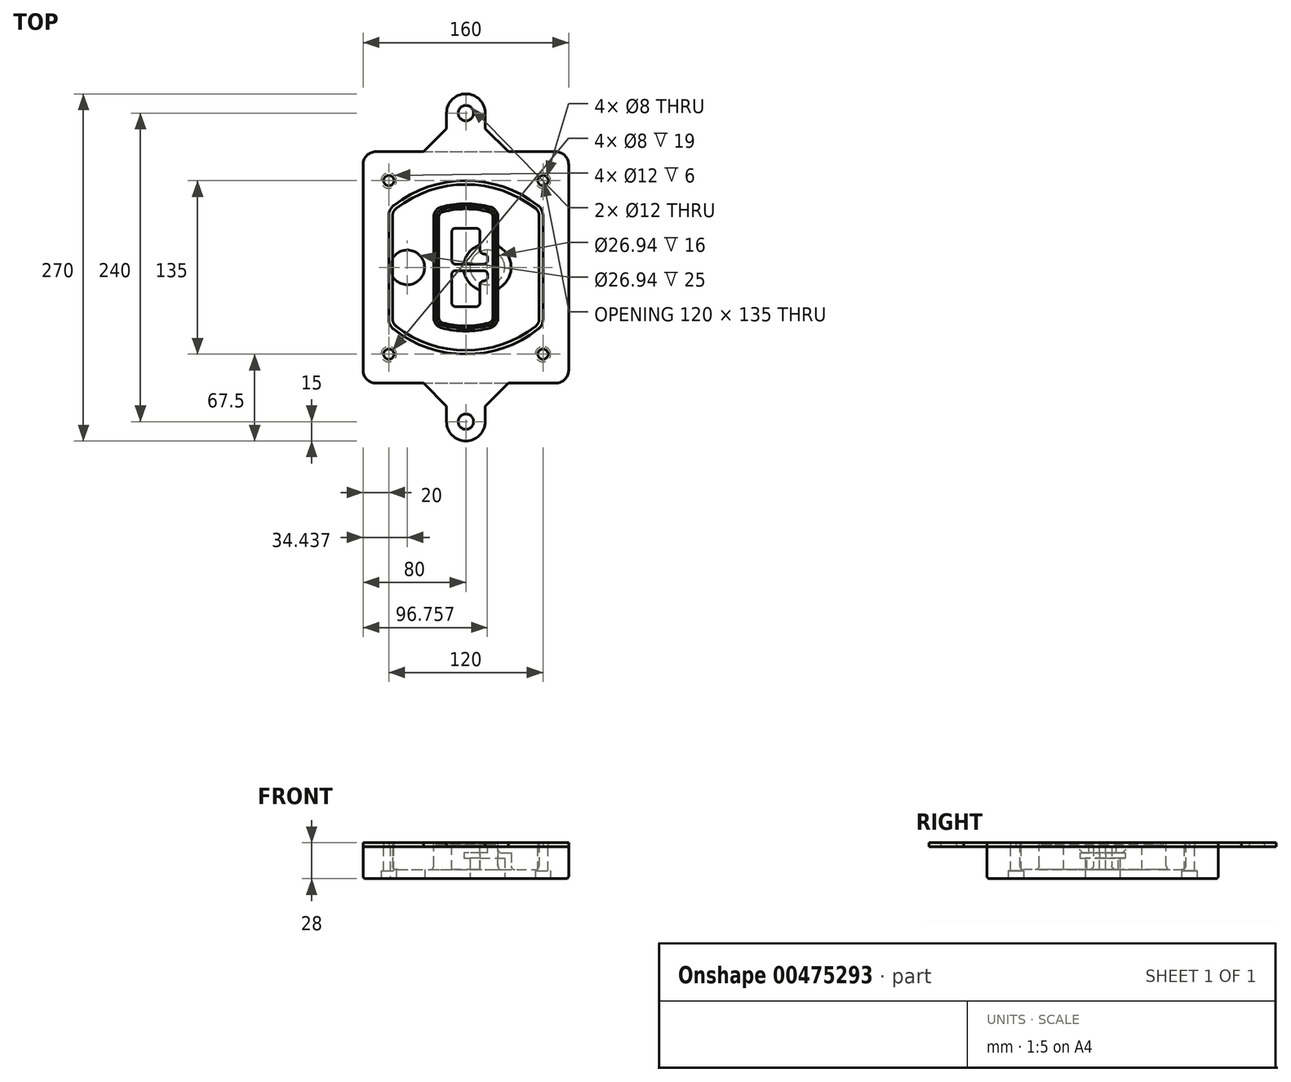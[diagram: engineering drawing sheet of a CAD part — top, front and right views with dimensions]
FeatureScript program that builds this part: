
annotation { "Feature Type Name" : "Feature", "Feature Type Description" : "" }
export const myFeature = defineFeature(function(context is Context, id is Id, definition is map)
    precondition{}
    {
        {
            var Q0;
            Q0=qCreatedBy(makeId("Top.planeOp"),FACE);
            var sketch = newSketch(context, id + "F0", { "sketchPlane" : qUnion([Q0])});
            skPoint(sketch, "E0.rect.middle", {"position": v(0, 0) * mm});
            skLineSegment(sketch, "E1.bottom", {"start": v(-70, -90) * mm, "end": v(70, -90) * mm});
            skLineSegment(sketch, "E1.top", {"start": v(-70, 90) * mm, "end": v(70, 90) * mm});
            skLineSegment(sketch, "E1.left", {"start": v(-80, -80) * mm, "end": v(-80, 80) * mm});
            skLineSegment(sketch, "E1.right", {"start": v(80, -80) * mm, "end": v(80, 80) * mm});
            skLineSegment(sketch, "E2", {"start": v(-80, 90) * mm, "end": v(80, -90) * mm, "construction": true});
            skLineSegment(sketch, "E3", {"start": v(80, 90) * mm, "end": v(-80, -90) * mm, "construction": true});
            skCircle(sketch, "E4", {"center": v(-60, 67.5) * mm, "radius": 4 * mm});
            skCircle(sketch, "E5", {"center": v(60, 67.5) * mm, "radius": 4 * mm});
            skCircle(sketch, "E6", {"center": v(60, -67.5) * mm, "radius": 4 * mm});
            skCircle(sketch, "E7", {"center": v(-60, -67.5) * mm, "radius": 4 * mm});
            skLineSegment(sketch, "E8", {"start": v(-60, 67.5) * mm, "end": v(60, 67.5) * mm, "construction": true});
            skLineSegment(sketch, "E9", {"start": v(60, 67.5) * mm, "end": v(60, -67.5) * mm, "construction": true});
            skLineSegment(sketch, "E10", {"start": v(60, -67.5) * mm, "end": v(-60, -67.5) * mm, "construction": true});
            skLineSegment(sketch, "E11", {"start": v(-60, -67.5) * mm, "end": v(-60, 67.5) * mm, "construction": true});
            skLineSegment(sketch, "E12", {"start": v(-60, 40.3) * mm, "end": v(-60, -40.3) * mm});
            skLineSegment(sketch, "E13", {"start": v(60, 40.3) * mm, "end": v(60, -40.3) * mm});
            skArc(sketch, "E14", {"start": v(56.15, 48.18) * mm, "mid": v(0, 67.5) * mm, "end": v(-56.15, 48.18) * mm});
            skArc(sketch, "E15", {"start": v(-56.15, -48.18) * mm, "mid": v(0, -67.5) * mm, "end": v(56.15, -48.18) * mm});
            skLineSegment(sketch, "E16", {"start": v(-60, 0) * mm, "end": v(60, 0) * mm, "construction": true});
            skPoint(sketch, "E17.visualSharp", {"position": v(-60, -45) * mm});
            skArc(sketch, "E17.filletArc", {"start": v(-60, -40.3) * mm, "mid": v(-58.99, -44.68) * mm, "end": v(-56.15, -48.18) * mm});
            skPoint(sketch, "E18.visualSharp", {"position": v(-60, 45) * mm});
            skArc(sketch, "E18.filletArc", {"start": v(-56.15, 48.18) * mm, "mid": v(-58.99, 44.68) * mm, "end": v(-60, 40.3) * mm});
            skPoint(sketch, "E19.visualSharp", {"position": v(60, 45) * mm});
            skArc(sketch, "E19.filletArc", {"start": v(60, 40.3) * mm, "mid": v(58.99, 44.68) * mm, "end": v(56.15, 48.18) * mm});
            skPoint(sketch, "E20.visualSharp", {"position": v(60, -45) * mm});
            skArc(sketch, "E20.filletArc", {"start": v(56.15, -48.18) * mm, "mid": v(58.99, -44.68) * mm, "end": v(60, -40.3) * mm});
            skPoint(sketch, "E21.visualSharp", {"position": v(-80, 90) * mm});
            skArc(sketch, "E21.filletArc", {"start": v(-70, 90) * mm, "mid": v(-77.07, 87.07) * mm, "end": v(-80, 80) * mm});
            skPoint(sketch, "E22.visualSharp", {"position": v(80, 90) * mm});
            skArc(sketch, "E22.filletArc", {"start": v(80, 80) * mm, "mid": v(77.07, 87.07) * mm, "end": v(70, 90) * mm});
            skPoint(sketch, "E23.visualSharp", {"position": v(80, -90) * mm});
            skArc(sketch, "E23.filletArc", {"start": v(70, -90) * mm, "mid": v(77.07, -87.07) * mm, "end": v(80, -80) * mm});
            skPoint(sketch, "E24.visualSharp", {"position": v(-80, -90) * mm});
            skArc(sketch, "E24.filletArc", {"start": v(-80, -80) * mm, "mid": v(-77.07, -87.07) * mm, "end": v(-70, -90) * mm});
            skArc(sketch, "E25.0", {"start": v(57, 40.3) * mm, "mid": v(56.3, 43.36) * mm, "end": v(54.3, 45.81) * mm});
            skLineSegment(sketch, "E25.1", {"start": v(57, 40.3) * mm, "end": v(57, -40.3) * mm});
            skArc(sketch, "E25.2", {"start": v(54.3, -45.81) * mm, "mid": v(56.3, -43.36) * mm, "end": v(57, -40.3) * mm});
            skArc(sketch, "E25.3", {"start": v(-54.3, -45.81) * mm, "mid": v(0, -64.5) * mm, "end": v(54.3, -45.81) * mm});
            skArc(sketch, "E25.4", {"start": v(-57, -40.3) * mm, "mid": v(-56.3, -43.36) * mm, "end": v(-54.3, -45.81) * mm});
            skArc(sketch, "E25.5", {"start": v(54.3, 45.81) * mm, "mid": v(0, 64.5) * mm, "end": v(-54.3, 45.81) * mm});
            skLineSegment(sketch, "E25.6", {"start": v(-57, 40.3) * mm, "end": v(-57, -40.3) * mm});
            skArc(sketch, "E25.7", {"start": v(-54.3, 45.81) * mm, "mid": v(-56.3, 43.36) * mm, "end": v(-57, 40.3) * mm});
            skArc(sketch, "E26.0", {"start": v(-58.62, 51.33) * mm, "mid": v(-62.58, 46.43) * mm, "end": v(-64, 40.3) * mm});
            skArc(sketch, "E26.1", {"start": v(58.62, 51.33) * mm, "mid": v(0, 71.5) * mm, "end": v(-58.62, 51.33) * mm});
            skArc(sketch, "E26.2", {"start": v(64, 40.3) * mm, "mid": v(62.58, 46.43) * mm, "end": v(58.62, 51.33) * mm});
            skLineSegment(sketch, "E26.3", {"start": v(64, 40.3) * mm, "end": v(64, -40.3) * mm});
            skArc(sketch, "E26.4", {"start": v(58.62, -51.33) * mm, "mid": v(62.58, -46.43) * mm, "end": v(64, -40.3) * mm});
            skLineSegment(sketch, "E26.5", {"start": v(-64, 40.3) * mm, "end": v(-64, -40.3) * mm});
            skArc(sketch, "E26.6", {"start": v(-58.62, -51.33) * mm, "mid": v(0, -71.5) * mm, "end": v(58.62, -51.33) * mm});
            skArc(sketch, "E26.7", {"start": v(-64, -40.3) * mm, "mid": v(-62.58, -46.43) * mm, "end": v(-58.62, -51.33) * mm});
            skSolve(sketch);
        }
        {
            var Q0;
            Q0=makeQuery(id+"F0.imprint","IMPRINT",FACE,{"disambiguationData":[TD([[makeQuery(id+"F0.imprint","IMPRINT",EDGE,{"derivedFrom":sQuery(id+"F0.wireOp",EDGE,"E1.bottom")}),1.0]])]});
            var Q1;
            Q1=makeQuery(id+"F0.imprint","IMPRINT",FACE,{"disambiguationData":[TD([[makeQuery(id+"F0.imprint","IMPRINT",EDGE,{"derivedFrom":sQuery(id+"F0.wireOp",EDGE,"E12")}),1.0]])]});
            var Q2;
            Q2=makeQuery(id+"F0.imprint","IMPRINT",FACE,{"disambiguationData":[TD([[makeQuery(id+"F0.imprint","IMPRINT",EDGE,{"derivedFrom":sQuery(id+"F0.wireOp",EDGE,"E25.0")}),1.0]])]});
            var Q3;
            Q3=makeQuery(id+"F0.imprint","IMPRINT",FACE,{"disambiguationData":[TD([[makeQuery(id+"F0.imprint","IMPRINT",EDGE,{"derivedFrom":sQuery(id+"F0.wireOp",EDGE,"E12")}),-1.0]])]});
            extrude(context, id + "F1", {"entities" : qUnion([Q0, Q1, Q2, Q3]), "oppositeDirection" : true, "depth" : 25 * mm});
        }
        {
            var Q0;
            Q0=makeQuery(id+"F0.imprint","IMPRINT",FACE,{"disambiguationData":[TD([[makeQuery(id+"F0.imprint","IMPRINT",EDGE,{"derivedFrom":sQuery(id+"F0.wireOp",EDGE,"E12")}),1.0]])]});
            extrude(context, id + "F2", {"entities" : qUnion([Q0]), "operationType" : NewBodyOperationType.ADD, "depth" : 3 * mm});
        }
        {
            var Q0;
            Q0=makeQuery(id+"F0.imprint","IMPRINT",FACE,{"disambiguationData":[TD([[makeQuery(id+"F0.imprint","IMPRINT",EDGE,{"derivedFrom":sQuery(id+"F0.wireOp",EDGE,"E25.0")}),1.0]])]});
            extrude(context, id + "F3", {"entities" : qUnion([Q0]), "operationType" : NewBodyOperationType.REMOVE, "oppositeDirection" : true, "depth" : 18 * mm});
        }
        {
            var Q0;
            Q0=makeQuery(id+"F2.opExtrude","CAP_FACE",FACE,{"disambiguationData":[OSD([sQuery(id+"F0.wireOp",EDGE,"E12"),sQuery(id+"F0.wireOp",EDGE,"E13"),sQuery(id+"F0.wireOp",EDGE,"E14"),sQuery(id+"F0.wireOp",EDGE,"E15"),sQuery(id+"F0.wireOp",EDGE,"E17.filletArc"),sQuery(id+"F0.wireOp",EDGE,"E18.filletArc"),sQuery(id+"F0.wireOp",EDGE,"E19.filletArc"),sQuery(id+"F0.wireOp",EDGE,"E20.filletArc"),sQuery(id+"F0.wireOp",EDGE,"E25.0"),sQuery(id+"F0.wireOp",EDGE,"E25.1"),sQuery(id+"F0.wireOp",EDGE,"E25.2"),sQuery(id+"F0.wireOp",EDGE,"E25.3"),sQuery(id+"F0.wireOp",EDGE,"E25.4"),sQuery(id+"F0.wireOp",EDGE,"E25.5"),sQuery(id+"F0.wireOp",EDGE,"E25.6"),sQuery(id+"F0.wireOp",EDGE,"E25.7")])],"isStart":false});
            var sketch = newSketch(context, id + "F4", { "sketchPlane" : qUnion([Q0])});
            skArc(sketch, "E27.0", {"start": v(-19.08, -46.97) * mm, "mid": v(0, -49.5) * mm, "end": v(19.08, -46.97) * mm});
            skArc(sketch, "E28.0", {"start": v(19.08, 46.97) * mm, "mid": v(0, 49.5) * mm, "end": v(-19.08, 46.97) * mm});
            skLineSegment(sketch, "E29", {"start": v(-25, 39.25) * mm, "end": v(-25, -39.25) * mm});
            skLineSegment(sketch, "E30", {"start": v(25, 39.25) * mm, "end": v(25, -39.25) * mm});
            skLineSegment(sketch, "E31", {"start": v(-25, 45.1) * mm, "end": v(25, 45.1) * mm, "construction": true});
            skLineSegment(sketch, "E32", {"start": v(-25, -45.1) * mm, "end": v(25, -45.1) * mm, "construction": true});
            skPoint(sketch, "E33.visualSharp", {"position": v(-25, 45.1) * mm});
            skArc(sketch, "E33.filletArc", {"start": v(-19.08, 46.97) * mm, "mid": v(-23.35, 44.11) * mm, "end": v(-25, 39.25) * mm});
            skPoint(sketch, "E34.visualSharp", {"position": v(25, 45.1) * mm});
            skArc(sketch, "E34.filletArc", {"start": v(25, 39.25) * mm, "mid": v(23.35, 44.11) * mm, "end": v(19.08, 46.97) * mm});
            skPoint(sketch, "E35.visualSharp", {"position": v(25, -45.1) * mm});
            skArc(sketch, "E35.filletArc", {"start": v(19.08, -46.97) * mm, "mid": v(23.35, -44.11) * mm, "end": v(25, -39.25) * mm});
            skPoint(sketch, "E36.visualSharp", {"position": v(-25, -45.1) * mm});
            skArc(sketch, "E36.filletArc", {"start": v(-25, -39.25) * mm, "mid": v(-23.35, -44.11) * mm, "end": v(-19.08, -46.97) * mm});
            skArc(sketch, "E37.0", {"start": v(54.3, 45.81) * mm, "mid": v(0, 64.5) * mm, "end": v(-54.3, 45.81) * mm});
            skArc(sketch, "E37.1", {"start": v(-54.3, 45.81) * mm, "mid": v(-56.3, 43.36) * mm, "end": v(-57, 40.3) * mm});
            skLineSegment(sketch, "E37.2", {"start": v(-57, 40.3) * mm, "end": v(-57, -40.3) * mm});
            skArc(sketch, "E37.3", {"start": v(-57, -40.3) * mm, "mid": v(-56.3, -43.36) * mm, "end": v(-54.3, -45.81) * mm});
            skArc(sketch, "E37.4", {"start": v(-54.3, -45.81) * mm, "mid": v(0, -64.5) * mm, "end": v(54.3, -45.81) * mm});
            skArc(sketch, "E37.5", {"start": v(54.3, -45.81) * mm, "mid": v(56.3, -43.36) * mm, "end": v(57, -40.3) * mm});
            skLineSegment(sketch, "E37.6", {"start": v(57, 40.3) * mm, "end": v(57, -40.3) * mm});
            skArc(sketch, "E37.7", {"start": v(57, 40.3) * mm, "mid": v(56.3, 43.36) * mm, "end": v(54.3, 45.81) * mm});
            skLineSegment(sketch, "E38.0", {"start": v(23, 39.25) * mm, "end": v(23, -39.25) * mm});
            skArc(sketch, "E38.1", {"start": v(18.56, -45.04) * mm, "mid": v(21.76, -42.9) * mm, "end": v(23, -39.25) * mm});
            skArc(sketch, "E38.2", {"start": v(-18.56, -45.04) * mm, "mid": v(0, -47.5) * mm, "end": v(18.56, -45.04) * mm});
            skArc(sketch, "E38.3", {"start": v(-23, -39.25) * mm, "mid": v(-21.76, -42.9) * mm, "end": v(-18.56, -45.04) * mm});
            skLineSegment(sketch, "E38.4", {"start": v(-23, 39.25) * mm, "end": v(-23, -39.25) * mm});
            skArc(sketch, "E38.5", {"start": v(23, 39.25) * mm, "mid": v(21.76, 42.9) * mm, "end": v(18.56, 45.04) * mm});
            skArc(sketch, "E38.6", {"start": v(-18.56, 45.04) * mm, "mid": v(-21.76, 42.9) * mm, "end": v(-23, 39.25) * mm});
            skArc(sketch, "E38.7", {"start": v(18.56, 45.04) * mm, "mid": v(0, 47.5) * mm, "end": v(-18.56, 45.04) * mm});
            skArc(sketch, "E39.0", {"start": v(21, 39.25) * mm, "mid": v(20.18, 41.68) * mm, "end": v(18.04, 43.1) * mm});
            skLineSegment(sketch, "E39.1", {"start": v(21, 39.25) * mm, "end": v(21, -39.25) * mm});
            skArc(sketch, "E39.2", {"start": v(18.04, -43.1) * mm, "mid": v(20.18, -41.68) * mm, "end": v(21, -39.25) * mm});
            skArc(sketch, "E39.3", {"start": v(-18.04, -43.1) * mm, "mid": v(0, -45.5) * mm, "end": v(18.04, -43.1) * mm});
            skArc(sketch, "E39.4", {"start": v(-21, -39.25) * mm, "mid": v(-20.18, -41.68) * mm, "end": v(-18.04, -43.1) * mm});
            skArc(sketch, "E39.5", {"start": v(18.04, 43.1) * mm, "mid": v(0, 45.5) * mm, "end": v(-18.04, 43.1) * mm});
            skLineSegment(sketch, "E39.6", {"start": v(-21, 39.25) * mm, "end": v(-21, -39.25) * mm});
            skArc(sketch, "E39.7", {"start": v(-18.04, 43.1) * mm, "mid": v(-20.18, 41.68) * mm, "end": v(-21, 39.25) * mm});
            skLineSegment(sketch, "E40", {"start": v(-25, 0) * mm, "end": v(25, 0) * mm, "construction": true});
            skLineSegment(sketch, "E41", {"start": v(-11, 5.5) * mm, "end": v(-11, 27.5) * mm});
            skLineSegment(sketch, "E42", {"start": v(-8, 30.5) * mm, "end": v(8, 30.5) * mm});
            skLineSegment(sketch, "E43", {"start": v(11, 27.5) * mm, "end": v(11, 13.5) * mm});
            skLineSegment(sketch, "E44", {"start": v(14, 10.5) * mm, "end": v(14, 10.5) * mm});
            skLineSegment(sketch, "E45", {"start": v(17, 7.5) * mm, "end": v(17, 5.5) * mm});
            skLineSegment(sketch, "E46", {"start": v(14, 2.5) * mm, "end": v(-8, 2.5) * mm});
            skPoint(sketch, "E47.visualSharp", {"position": v(-11, 30.5) * mm});
            skArc(sketch, "E47.filletArc", {"start": v(-8, 30.5) * mm, "mid": v(-10.12, 29.62) * mm, "end": v(-11, 27.5) * mm});
            skPoint(sketch, "E48.visualSharp", {"position": v(11, 30.5) * mm});
            skArc(sketch, "E48.filletArc", {"start": v(11, 27.5) * mm, "mid": v(10.12, 29.62) * mm, "end": v(8, 30.5) * mm});
            skPoint(sketch, "E49.visualSharp", {"position": v(11, 10.5) * mm});
            skArc(sketch, "E49.filletArc", {"start": v(11, 13.5) * mm, "mid": v(11.88, 11.38) * mm, "end": v(14, 10.5) * mm});
            skPoint(sketch, "E50.visualSharp", {"position": v(17, 10.5) * mm});
            skArc(sketch, "E50.filletArc", {"start": v(17, 7.5) * mm, "mid": v(16.12, 9.62) * mm, "end": v(14, 10.5) * mm});
            skPoint(sketch, "E51.visualSharp", {"position": v(17, 2.5) * mm});
            skArc(sketch, "E51.filletArc", {"start": v(14, 2.5) * mm, "mid": v(16.12, 3.38) * mm, "end": v(17, 5.5) * mm});
            skPoint(sketch, "E52.visualSharp", {"position": v(-11, 2.5) * mm});
            skArc(sketch, "E52.filletArc", {"start": v(-11, 5.5) * mm, "mid": v(-10.12, 3.38) * mm, "end": v(-8, 2.5) * mm});
            skLineSegment(sketch, "E53.0.MirrorCS", {"start": v(14, -2.5) * mm, "end": v(-8, -2.5) * mm});
            skArc(sketch, "E54.0.MirrorCS", {"start": v(-11, -5.5) * mm, "mid": v(-10.12, -3.38) * mm, "end": v(-8, -2.5) * mm});
            skLineSegment(sketch, "E55.0.MirrorCS", {"start": v(-11, -5.5) * mm, "end": v(-11, -27.5) * mm});
            skArc(sketch, "E56.0.MirrorCS", {"start": v(-8, -30.5) * mm, "mid": v(-10.12, -29.62) * mm, "end": v(-11, -27.5) * mm});
            skLineSegment(sketch, "E57.0.MirrorCS", {"start": v(-8, -30.5) * mm, "end": v(8, -30.5) * mm});
            skArc(sketch, "E58.0.MirrorCS", {"start": v(11, -27.5) * mm, "mid": v(10.12, -29.62) * mm, "end": v(8, -30.5) * mm});
            skLineSegment(sketch, "E59.0.MirrorCS", {"start": v(11, -27.5) * mm, "end": v(11, -13.5) * mm});
            skArc(sketch, "E60.0.MirrorCS", {"start": v(11, -13.5) * mm, "mid": v(11.88, -11.38) * mm, "end": v(14, -10.5) * mm});
            skArc(sketch, "E61.0.MirrorCS", {"start": v(17, -7.5) * mm, "mid": v(16.12, -9.62) * mm, "end": v(14, -10.5) * mm});
            skLineSegment(sketch, "E62.0.MirrorCS", {"start": v(17, -7.5) * mm, "end": v(17, -5.5) * mm});
            skArc(sketch, "E63.0.MirrorCS", {"start": v(14, -2.5) * mm, "mid": v(16.12, -3.38) * mm, "end": v(17, -5.5) * mm});
            skSolve(sketch);
        }
        {
            var Q0;
            Q0=makeQuery(id+"F4.imprint","IMPRINT",FACE,{"disambiguationData":[TD([[makeQuery(id+"F4.imprint","IMPRINT",EDGE,{"derivedFrom":sQuery(id+"F4.wireOp",EDGE,"E27.0")}),1.0]])]});
            var Q1;
            Q1=makeQuery(id+"F4.imprint","IMPRINT",FACE,{"disambiguationData":[TD([[makeQuery(id+"F4.imprint","IMPRINT",EDGE,{"derivedFrom":sQuery(id+"F4.wireOp",EDGE,"E38.0")}),-1.0]])]});
            var Q2;
            Q2=makeQuery(id+"F4.imprint","IMPRINT",FACE,{"disambiguationData":[TD([[makeQuery(id+"F4.imprint","IMPRINT",EDGE,{"derivedFrom":sQuery(id+"F4.wireOp",EDGE,"E39.0")}),1.0]])]});
            extrude(context, id + "F5", {"entities" : qUnion([Q0, Q1, Q2]), "operationType" : NewBodyOperationType.ADD, "endBound" : BoundingType.UP_TO_NEXT, "oppositeDirection" : true, "depth" : 25 * mm});
        }
        {
            var Q0;
            Q0=makeQuery(id+"F4.imprint","IMPRINT",FACE,{"disambiguationData":[TD([[makeQuery(id+"F4.imprint","IMPRINT",EDGE,{"derivedFrom":sQuery(id+"F4.wireOp",EDGE,"E38.0")}),-1.0]])]});
            extrude(context, id + "F6", {"entities" : qUnion([Q0]), "operationType" : NewBodyOperationType.REMOVE, "oppositeDirection" : true, "depth" : 2 * mm});
        }
        {
            var Q0;
            Q0=makeQuery(id+"F1.opExtrude","CAP_FACE",FACE,{"disambiguationData":[OSD([sQuery(id+"F0.wireOp",EDGE,"E1.bottom"),sQuery(id+"F0.wireOp",EDGE,"E1.top"),sQuery(id+"F0.wireOp",EDGE,"E1.left"),sQuery(id+"F0.wireOp",EDGE,"E1.right"),sQuery(id+"F0.wireOp",EDGE,"E4"),sQuery(id+"F0.wireOp",EDGE,"E5"),sQuery(id+"F0.wireOp",EDGE,"E6"),sQuery(id+"F0.wireOp",EDGE,"E7"),sQuery(id+"F0.wireOp",EDGE,"E21.filletArc"),sQuery(id+"F0.wireOp",EDGE,"E22.filletArc"),sQuery(id+"F0.wireOp",EDGE,"E23.filletArc"),sQuery(id+"F0.wireOp",EDGE,"E24.filletArc")])],"isStart":false});
            var sketch = newSketch(context, id + "F7", { "sketchPlane" : qUnion([Q0])});
            skCircle(sketch, "E64", {"center": v(16.76, 0) * mm, "radius": 13.47 * mm});
            skCircle(sketch, "E65", {"center": v(-45.56, 0) * mm, "radius": 13.47 * mm});
            skLineSegment(sketch, "E66", {"start": v(80, 0) * mm, "end": v(-80, 0) * mm});
            skCircle(sketch, "E67", {"center": v(16.76, 0) * mm, "radius": 18.47 * mm});
            skCircle(sketch, "E68", {"center": v(60, -67.5) * mm, "radius": 6 * mm});
            skCircle(sketch, "E69", {"center": v(-60, -67.5) * mm, "radius": 6 * mm});
            skCircle(sketch, "E70", {"center": v(-60, 67.5) * mm, "radius": 6 * mm});
            skCircle(sketch, "E71", {"center": v(60, 67.5) * mm, "radius": 6 * mm});
            skSolve(sketch);
        }
        {
            var Q0;
            {var subQ1=sQuery(id+"F7.wireOp",EDGE,"E66");var subQ4=sQuery(id+"F7.wireOp",EDGE,"E64");var subQ6=makeQuery(id+"F7.imprint","INTERSECT",VERTEX,{"disambiguationData":[OD(0.0)],"derivedFrom":[subQ4,subQ1]});Q0=makeQuery(id+"F7.imprint","IMPRINT",FACE,{"disambiguationData":[TD([[makeQuery(id+"F7.imprint","IMPRINT",EDGE,{"disambiguationData":[TD([[subQ6,-1.0]])],"derivedFrom":subQ4}),-1.0]])]});}
            var Q1;
            {var subQ0=sQuery(id+"F7.wireOp",EDGE,"E66");var subQ1=sQuery(id+"F7.wireOp",EDGE,"E64");var subQ3=makeQuery(id+"F7.imprint","INTERSECT",VERTEX,{"disambiguationData":[OD(0.0)],"derivedFrom":[subQ1,subQ0]});Q1=makeQuery(id+"F7.imprint","IMPRINT",FACE,{"disambiguationData":[TD([[makeQuery(id+"F7.imprint","IMPRINT",EDGE,{"disambiguationData":[TD([[subQ3,-1.0]])],"derivedFrom":subQ1}),1.0]])]});}
            var Q2;
            {var subQ0=sQuery(id+"F7.wireOp",EDGE,"E66");var subQ1=sQuery(id+"F7.wireOp",EDGE,"E64");var subQ3=makeQuery(id+"F7.imprint","INTERSECT",VERTEX,{"disambiguationData":[OD(0.0)],"derivedFrom":[subQ1,subQ0]});Q2=makeQuery(id+"F7.imprint","IMPRINT",FACE,{"disambiguationData":[TD([[makeQuery(id+"F7.imprint","IMPRINT",EDGE,{"disambiguationData":[TD([[subQ3,1.0]])],"derivedFrom":subQ1}),1.0]])]});}
            var Q3;
            {var subQ1=sQuery(id+"F7.wireOp",EDGE,"E66");var subQ4=sQuery(id+"F7.wireOp",EDGE,"E64");var subQ6=makeQuery(id+"F7.imprint","INTERSECT",VERTEX,{"disambiguationData":[OD(0.0)],"derivedFrom":[subQ4,subQ1]});Q3=makeQuery(id+"F7.imprint","IMPRINT",FACE,{"disambiguationData":[TD([[makeQuery(id+"F7.imprint","IMPRINT",EDGE,{"disambiguationData":[TD([[subQ6,1.0]])],"derivedFrom":subQ4}),-1.0]])]});}
            extrude(context, id + "F8", {"entities" : qUnion([Q0, Q1, Q2, Q3]), "operationType" : NewBodyOperationType.ADD, "oppositeDirection" : true, "depth" : 20 * mm});
        }
        {
            var Q0;
            {var subQ0=sQuery(id+"F7.wireOp",EDGE,"E66");var subQ1=sQuery(id+"F7.wireOp",EDGE,"E64");var subQ3=makeQuery(id+"F7.imprint","INTERSECT",VERTEX,{"disambiguationData":[OD(0.0)],"derivedFrom":[subQ1,subQ0]});Q0=makeQuery(id+"F7.imprint","IMPRINT",FACE,{"disambiguationData":[TD([[makeQuery(id+"F7.imprint","IMPRINT",EDGE,{"disambiguationData":[TD([[subQ3,-1.0]])],"derivedFrom":subQ1}),1.0]])]});}
            var Q1;
            {var subQ0=sQuery(id+"F7.wireOp",EDGE,"E66");var subQ1=sQuery(id+"F7.wireOp",EDGE,"E64");var subQ3=makeQuery(id+"F7.imprint","INTERSECT",VERTEX,{"disambiguationData":[OD(0.0)],"derivedFrom":[subQ1,subQ0]});Q1=makeQuery(id+"F7.imprint","IMPRINT",FACE,{"disambiguationData":[TD([[makeQuery(id+"F7.imprint","IMPRINT",EDGE,{"disambiguationData":[TD([[subQ3,1.0]])],"derivedFrom":subQ1}),1.0]])]});}
            extrude(context, id + "F9", {"entities" : qUnion([Q0, Q1]), "operationType" : NewBodyOperationType.REMOVE, "oppositeDirection" : true, "depth" : 16 * mm});
        }
        {
            var Q0;
            {var subQ0=sQuery(id+"F7.wireOp",EDGE,"E66");var subQ1=sQuery(id+"F7.wireOp",EDGE,"E65");var subQ3=makeQuery(id+"F7.imprint","INTERSECT",VERTEX,{"disambiguationData":[OD(0.0)],"derivedFrom":[subQ1,subQ0]});Q0=makeQuery(id+"F7.imprint","IMPRINT",FACE,{"disambiguationData":[TD([[makeQuery(id+"F7.imprint","IMPRINT",EDGE,{"disambiguationData":[TD([[subQ3,-1.0]])],"derivedFrom":subQ1}),1.0]])]});}
            var Q1;
            {var subQ0=sQuery(id+"F7.wireOp",EDGE,"E66");var subQ1=sQuery(id+"F7.wireOp",EDGE,"E65");var subQ3=makeQuery(id+"F7.imprint","INTERSECT",VERTEX,{"disambiguationData":[OD(0.0)],"derivedFrom":[subQ1,subQ0]});Q1=makeQuery(id+"F7.imprint","IMPRINT",FACE,{"disambiguationData":[TD([[makeQuery(id+"F7.imprint","IMPRINT",EDGE,{"disambiguationData":[TD([[subQ3,1.0]])],"derivedFrom":subQ1}),1.0]])]});}
            extrude(context, id + "F10", {"entities" : qUnion([Q0, Q1]), "operationType" : NewBodyOperationType.REMOVE, "oppositeDirection" : true, "depth" : 25 * mm});
        }
        {
            var Q0;
            Q0=makeQuery(id+"F7.imprint","IMPRINT",FACE,{"disambiguationData":[TD([[makeQuery(id+"F7.imprint","IMPRINT",EDGE,{"derivedFrom":sQuery(id+"F7.wireOp",EDGE,"E68")}),1.0]])]});
            var Q1;
            Q1=makeQuery(id+"F7.imprint","IMPRINT",FACE,{"disambiguationData":[TD([[makeQuery(id+"F7.imprint","IMPRINT",EDGE,{"derivedFrom":makeQuery(id+"F1.opExtrude","CAP_EDGE",EDGE,{"disambiguationData":[OSD([sQuery(id+"F0.wireOp",EDGE,"E5")])],"isStart":false})}),-1.0]])]});
            var Q2;
            Q2=makeQuery(id+"F7.imprint","IMPRINT",FACE,{"disambiguationData":[TD([[makeQuery(id+"F7.imprint","IMPRINT",EDGE,{"derivedFrom":sQuery(id+"F7.wireOp",EDGE,"E69")}),1.0]])]});
            var Q3;
            Q3=makeQuery(id+"F7.imprint","IMPRINT",FACE,{"disambiguationData":[TD([[makeQuery(id+"F7.imprint","IMPRINT",EDGE,{"derivedFrom":makeQuery(id+"F1.opExtrude","CAP_EDGE",EDGE,{"disambiguationData":[OSD([sQuery(id+"F0.wireOp",EDGE,"E4")])],"isStart":false})}),-1.0]])]});
            var Q4;
            Q4=makeQuery(id+"F7.imprint","IMPRINT",FACE,{"disambiguationData":[TD([[makeQuery(id+"F7.imprint","IMPRINT",EDGE,{"derivedFrom":sQuery(id+"F7.wireOp",EDGE,"E70")}),1.0]])]});
            var Q5;
            Q5=makeQuery(id+"F7.imprint","IMPRINT",FACE,{"disambiguationData":[TD([[makeQuery(id+"F7.imprint","IMPRINT",EDGE,{"derivedFrom":makeQuery(id+"F1.opExtrude","CAP_EDGE",EDGE,{"disambiguationData":[OSD([sQuery(id+"F0.wireOp",EDGE,"E7")])],"isStart":false})}),-1.0]])]});
            var Q6;
            Q6=makeQuery(id+"F7.imprint","IMPRINT",FACE,{"disambiguationData":[TD([[makeQuery(id+"F7.imprint","IMPRINT",EDGE,{"derivedFrom":sQuery(id+"F7.wireOp",EDGE,"E71")}),1.0]])]});
            var Q7;
            Q7=makeQuery(id+"F7.imprint","IMPRINT",FACE,{"disambiguationData":[TD([[makeQuery(id+"F7.imprint","IMPRINT",EDGE,{"derivedFrom":makeQuery(id+"F1.opExtrude","CAP_EDGE",EDGE,{"disambiguationData":[OSD([sQuery(id+"F0.wireOp",EDGE,"E6")])],"isStart":false})}),-1.0]])]});
            extrude(context, id + "F11", {"entities" : qUnion([Q0, Q1, Q2, Q3, Q4, Q5, Q6, Q7]), "operationType" : NewBodyOperationType.REMOVE, "oppositeDirection" : true, "depth" : 6 * mm});
        }
        {
            var Q0;
            Q0=makeQuery(id+"F9.boolean.opBoolean","COPY",FACE,{"derivedFrom":makeQuery(id+"F9.opExtrude","CAP_FACE",FACE,{"disambiguationData":[OSD([sQuery(id+"F7.wireOp",EDGE,"E64")])],"isStart":false})});
            var sketch = newSketch(context, id + "F12", { "sketchPlane" : qUnion([Q0])});
            skArc(sketch, "E72.0", {"start": v(11, 17.55) * mm, "mid": v(2.57, 11.82) * mm, "end": v(-1.54, 2.5) * mm});
            skArc(sketch, "E72.1", {"start": v(-1.54, -2.5) * mm, "mid": v(2.57, -11.82) * mm, "end": v(11, -17.55) * mm});
            skLineSegment(sketch, "E73", {"start": v(-1.54, -2.5) * mm, "end": v(14, -2.5) * mm});
            skLineSegment(sketch, "E74.0", {"start": v(14, 2.5) * mm, "end": v(-1.54, 2.5) * mm});
            skArc(sketch, "E74.1", {"start": v(14, 2.5) * mm, "mid": v(16.12, 3.38) * mm, "end": v(17, 5.5) * mm});
            skLineSegment(sketch, "E74.2", {"start": v(17, 7.5) * mm, "end": v(17, 5.5) * mm});
            skArc(sketch, "E74.3", {"start": v(17, 7.5) * mm, "mid": v(16.12, 9.62) * mm, "end": v(14, 10.5) * mm});
            skArc(sketch, "E74.4", {"start": v(11, 13.5) * mm, "mid": v(11.88, 11.38) * mm, "end": v(14, 10.5) * mm});
            skLineSegment(sketch, "E74.5", {"start": v(11, 17.55) * mm, "end": v(11, 13.5) * mm});
            skLineSegment(sketch, "E74.7", {"start": v(14, -2.5) * mm, "end": v(-1.54, -2.5) * mm});
            skArc(sketch, "E74.8", {"start": v(14, -2.5) * mm, "mid": v(16.12, -3.38) * mm, "end": v(17, -5.5) * mm});
            skLineSegment(sketch, "E74.9", {"start": v(17, -7.5) * mm, "end": v(17, -5.5) * mm});
            skArc(sketch, "E74.10", {"start": v(17, -7.5) * mm, "mid": v(16.12, -9.62) * mm, "end": v(14, -10.5) * mm});
            skArc(sketch, "E74.11", {"start": v(11, -13.5) * mm, "mid": v(11.88, -11.38) * mm, "end": v(14, -10.5) * mm});
            skLineSegment(sketch, "E74.12", {"start": v(11, -17.55) * mm, "end": v(11, -13.5) * mm});
            skPoint(sketch, "E75.orphan", {"position": v(11, -27.5) * mm});
            skPoint(sketch, "E76.orphan", {"position": v(-8, -2.5) * mm});
            skPoint(sketch, "E77.orphan", {"position": v(-8, 2.5) * mm});
            skPoint(sketch, "E78.orphan", {"position": v(11, 27.5) * mm});
            skSolve(sketch);
        }
        {
            var Q0;
            {var subQ7=sQuery(id+"F12.wireOp",EDGE,"E72.0");var subQ14=sQuery(id+"F12.wireOp",EDGE,"E72.1");var subQ16=sQuery(id+"F12.wireOp",EDGE,"E74.1");var subQ18=sQuery(id+"F12.wireOp",EDGE,"E74.8");Q0=qUnion([makeQuery(id+"F12.imprint","IMPRINT",FACE,{"disambiguationData":[TD([[makeQuery(id+"F12.imprint","IMPRINT",EDGE,{"derivedFrom":subQ7}),1.0]])]}),makeQuery(id+"F12.imprint","IMPRINT",FACE,{"disambiguationData":[TD([[makeQuery(id+"F12.imprint","IMPRINT",EDGE,{"derivedFrom":subQ14}),1.0]])]}),makeQuery(id+"F12.imprint","IMPRINT",FACE,{"disambiguationData":[TD([[makeQuery(id+"F12.imprint","IMPRINT",EDGE,{"derivedFrom":subQ16}),1.0]])]}),makeQuery(id+"F12.imprint","IMPRINT",FACE,{"disambiguationData":[TD([[makeQuery(id+"F12.imprint","IMPRINT",EDGE,{"derivedFrom":subQ18}),-1.0]])]})]);}
            var Q1;
            Q1=makeQuery(id+"F5.boolean.opBoolean","SPLIT",FACE,{"disambiguationData":[TD([makeQuery(id+"F5.opExtrude","SWEPT_FACE",FACE,{"disambiguationData":[OSD([sQuery(id+"F4.wireOp",EDGE,"E41")])]})])],"derivedFrom":makeQuery(id+"F3.boolean.opBoolean","COPY",FACE,{"derivedFrom":makeQuery(id+"F3.opExtrude","CAP_FACE",FACE,{"disambiguationData":[OSD([sQuery(id+"F0.wireOp",EDGE,"E25.0"),sQuery(id+"F0.wireOp",EDGE,"E25.1"),sQuery(id+"F0.wireOp",EDGE,"E25.2"),sQuery(id+"F0.wireOp",EDGE,"E25.3"),sQuery(id+"F0.wireOp",EDGE,"E25.4"),sQuery(id+"F0.wireOp",EDGE,"E25.5"),sQuery(id+"F0.wireOp",EDGE,"E25.6"),sQuery(id+"F0.wireOp",EDGE,"E25.7")])],"isStart":false})})});
            extrude(context, id + "F13", {"entities" : qUnion([Q0]), "operationType" : NewBodyOperationType.REMOVE, "endBound" : BoundingType.UP_TO_SURFACE, "endBoundEntityFace" : qUnion([Q1]), "depth" : 25 * mm});
        }
        {
            var Q0;
            Q0=makeQuery(id+"F3.boolean.opBoolean","COPY",EDGE,{"derivedFrom":makeQuery(id+"F3.opExtrude","CAP_EDGE",EDGE,{"disambiguationData":[OSD([sQuery(id+"F0.wireOp",EDGE,"E25.6")])],"isStart":false})});
            var Q1;
            Q1=makeQuery(id+"F8.boolean.opBoolean","INTERSECT",EDGE,{"derivedFrom":[makeQuery(id+"F5.opExtrude","SWEPT_FACE",FACE,{"disambiguationData":[OSD([sQuery(id+"F4.wireOp",EDGE,"E30")])]}),makeQuery(id+"F8.opExtrude","CAP_FACE",FACE,{"disambiguationData":[OSD([sQuery(id+"F7.wireOp",EDGE,"E67")])],"isStart":false})]});
            var Q2;
            Q2=makeQuery(id+"F8.boolean.opBoolean","INTERSECT",EDGE,{"disambiguationData":[OD(1.0)],"derivedFrom":[makeQuery(id+"F5.opExtrude","SWEPT_FACE",FACE,{"disambiguationData":[OSD([sQuery(id+"F4.wireOp",EDGE,"E30")])]}),makeQuery(id+"F8.opExtrude","SWEPT_FACE",FACE,{"disambiguationData":[OSD([sQuery(id+"F7.wireOp",EDGE,"E67")])]})]});
            var Q3;
            {var subQ0=sQuery(id+"F4.wireOp",EDGE,"E30");Q3=makeQuery(id+"F8.boolean.opBoolean","SPLIT",EDGE,{"disambiguationData":[TD([makeQuery(id+"F5.opExtrude","SWEPT_FACE",FACE,{"disambiguationData":[OSD([sQuery(id+"F4.wireOp",EDGE,"E35.filletArc")])]})])],"derivedFrom":makeQuery(id+"F5.opExtrude","CAP_EDGE",EDGE,{"disambiguationData":[OSD([subQ0])],"isStart":false})});}
            var Q4;
            {var subQ0=sQuery(id+"F0.wireOp",EDGE,"E25.7");var subQ1=sQuery(id+"F0.wireOp",EDGE,"E25.1");var subQ2=sQuery(id+"F0.wireOp",EDGE,"E25.6");var subQ3=sQuery(id+"F0.wireOp",EDGE,"E25.5");var subQ4=sQuery(id+"F0.wireOp",EDGE,"E25.4");var subQ5=sQuery(id+"F0.wireOp",EDGE,"E25.0");var subQ6=sQuery(id+"F0.wireOp",EDGE,"E25.2");var subQ7=sQuery(id+"F0.wireOp",EDGE,"E25.3");Q4=makeQuery(id+"F8.boolean.opBoolean","INTERSECT",EDGE,{"derivedFrom":[makeQuery(id+"F5.boolean.opBoolean","SPLIT",FACE,{"disambiguationData":[TD([makeQuery(id+"F2.opExtrude","SWEPT_FACE",FACE,{"disambiguationData":[OSD([subQ5])]})])],"derivedFrom":makeQuery(id+"F3.boolean.opBoolean","COPY",FACE,{"derivedFrom":makeQuery(id+"F3.opExtrude","CAP_FACE",FACE,{"disambiguationData":[OSD([subQ5,subQ1,subQ6,subQ7,subQ4,subQ3,subQ2,subQ0])],"isStart":false})})}),makeQuery(id+"F8.opExtrude","SWEPT_FACE",FACE,{"disambiguationData":[OSD([sQuery(id+"F7.wireOp",EDGE,"E67")])]})]});}
            var Q5;
            Q5=makeQuery(id+"F8.boolean.opBoolean","INTERSECT",EDGE,{"disambiguationData":[OD(0.0)],"derivedFrom":[makeQuery(id+"F5.opExtrude","SWEPT_FACE",FACE,{"disambiguationData":[OSD([sQuery(id+"F4.wireOp",EDGE,"E30")])]}),makeQuery(id+"F8.opExtrude","SWEPT_FACE",FACE,{"disambiguationData":[OSD([sQuery(id+"F7.wireOp",EDGE,"E67")])]})]});
            fillet(context, id + "F14", {"entities" : qUnion([Q0, Q1, Q2, Q3, Q4, Q5]), "radius" : 3 * mm, "tangentPropagation" : true, "allowEdgeOverflow" : false});
        }
        {
            var Q0;
            Q0=makeQuery(id+"F1.opExtrude","CAP_EDGE",EDGE,{"disambiguationData":[OSD([sQuery(id+"F0.wireOp",EDGE,"E1.bottom")])],"isStart":false});
            fillet(context, id + "F15", {"entities" : qUnion([Q0]), "radius" : 2 * mm, "tangentPropagation" : true, "allowEdgeOverflow" : false});
        }
        {
            var Q0;
            {var subQ0=sQuery(id+"F0.wireOp",EDGE,"E21.filletArc");var subQ1=sQuery(id+"F0.wireOp",EDGE,"E7");var subQ2=sQuery(id+"F0.wireOp",EDGE,"E6");var subQ3=sQuery(id+"F0.wireOp",EDGE,"E5");var subQ4=sQuery(id+"F0.wireOp",EDGE,"E4");var subQ5=sQuery(id+"F0.wireOp",EDGE,"E22.filletArc");var subQ6=sQuery(id+"F0.wireOp",EDGE,"E1.bottom");var subQ7=sQuery(id+"F0.wireOp",EDGE,"E1.right");var subQ8=sQuery(id+"F0.wireOp",EDGE,"E1.top");var subQ9=sQuery(id+"F0.wireOp",EDGE,"E1.left");var subQ10=sQuery(id+"F0.wireOp",EDGE,"E23.filletArc");var subQ11=sQuery(id+"F0.wireOp",EDGE,"E24.filletArc");Q0=makeQuery(id+"F2.boolean.opBoolean","SPLIT",FACE,{"disambiguationData":[TD([makeQuery(id+"F1.opExtrude","SWEPT_FACE",FACE,{"disambiguationData":[OSD([subQ6])]})])],"derivedFrom":makeQuery(id+"F1.opExtrude","CAP_FACE",FACE,{"disambiguationData":[OSD([subQ6,subQ8,subQ9,subQ7,subQ4,subQ3,subQ2,subQ1,subQ0,subQ5,subQ10,subQ11])],"isStart":true})});}
            var sketch = newSketch(context, id + "F16", { "sketchPlane" : qUnion([Q0])});
            skLineSegment(sketch, "E79.0", {"start": v(-70, 90) * mm, "end": v(70, 90) * mm});
            skArc(sketch, "E79.1", {"start": v(-70, 90) * mm, "mid": v(-77.07, 87.07) * mm, "end": v(-80, 80) * mm});
            skLineSegment(sketch, "E79.2", {"start": v(-80, -80) * mm, "end": v(-80, 80) * mm});
            skArc(sketch, "E79.3", {"start": v(-80, -80) * mm, "mid": v(-77.07, -87.07) * mm, "end": v(-70, -90) * mm});
            skLineSegment(sketch, "E79.4", {"start": v(-70, -90) * mm, "end": v(70, -90) * mm});
            skArc(sketch, "E79.5", {"start": v(70, -90) * mm, "mid": v(77.07, -87.07) * mm, "end": v(80, -80) * mm});
            skLineSegment(sketch, "E79.6", {"start": v(80, -80) * mm, "end": v(80, 80) * mm});
            skArc(sketch, "E79.7", {"start": v(80, 80) * mm, "mid": v(77.07, 87.07) * mm, "end": v(70, 90) * mm});
            skArc(sketch, "E79.8", {"start": v(56.15, 48.18) * mm, "mid": v(0, 67.5) * mm, "end": v(-56.15, 48.18) * mm});
            skArc(sketch, "E79.9", {"start": v(-56.15, -48.18) * mm, "mid": v(0, -67.5) * mm, "end": v(56.15, -48.18) * mm});
            skLineSegment(sketch, "E79.10", {"start": v(60, 40.3) * mm, "end": v(60, -40.3) * mm});
            skLineSegment(sketch, "E79.11", {"start": v(-60, 40.3) * mm, "end": v(-60, -40.3) * mm});
            skArc(sketch, "E79.12", {"start": v(-56.15, 48.18) * mm, "mid": v(-58.99, 44.68) * mm, "end": v(-60, 40.3) * mm});
            skArc(sketch, "E79.13", {"start": v(60, 40.3) * mm, "mid": v(58.99, 44.68) * mm, "end": v(56.15, 48.18) * mm});
            skArc(sketch, "E79.14", {"start": v(-60, -40.3) * mm, "mid": v(-58.99, -44.68) * mm, "end": v(-56.15, -48.18) * mm});
            skArc(sketch, "E79.15", {"start": v(56.15, -48.18) * mm, "mid": v(58.99, -44.68) * mm, "end": v(60, -40.3) * mm});
            skPoint(sketch, "E79.16", {"position": v(58.99, 44.68) * mm});
            skPoint(sketch, "E79.17", {"position": v(58.99, -44.68) * mm});
            skLineSegment(sketch, "E80.0", {"start": v(-70, 90) * mm, "end": v(70, 90) * mm, "construction": true});
            skLineSegment(sketch, "E81", {"start": v(0, 90) * mm, "end": v(0, 120) * mm, "construction": true});
            skPoint(sketch, "E81.endSnap0", {"position": v(0, 90) * mm});
            skLineSegment(sketch, "E82", {"start": v(15, 120) * mm, "end": v(15, 108) * mm});
            skLineSegment(sketch, "E83", {"start": v(-15, 108) * mm, "end": v(-33, 90) * mm});
            skLineSegment(sketch, "E84", {"start": v(15, 108) * mm, "end": v(33, 90) * mm});
            skLineSegment(sketch, "E85", {"start": v(-15, 108) * mm, "end": v(-15, 120) * mm});
            skArc(sketch, "E86", {"start": v(15, 120) * mm, "mid": v(0, 135) * mm, "end": v(-15, 120) * mm});
            skCircle(sketch, "E87", {"center": v(0, 120) * mm, "radius": 6 * mm});
            skLineSegment(sketch, "E88", {"start": v(-80, 0) * mm, "end": v(80, 0) * mm, "construction": true});
            skLineSegment(sketch, "E89.MirrorCS", {"start": v(-15, -108) * mm, "end": v(-33, -90) * mm});
            skLineSegment(sketch, "E90.MirrorCS", {"start": v(-15, -108) * mm, "end": v(-15, -120) * mm});
            skArc(sketch, "E91.MirrorCS", {"start": v(15, -120) * mm, "mid": v(0, -135) * mm, "end": v(-15, -120) * mm});
            skCircle(sketch, "E92.MirrorC", {"center": v(0, -120) * mm, "radius": 6 * mm});
            skLineSegment(sketch, "E93.MirrorCS", {"start": v(15, -120) * mm, "end": v(15, -108) * mm});
            skLineSegment(sketch, "E94.MirrorCS", {"start": v(15, -108) * mm, "end": v(33, -90) * mm});
            skLineSegment(sketch, "E95.MirrorCS", {"start": v(0, -90) * mm, "end": v(0, -120) * mm, "construction": true});
            skSolve(sketch);
        }
        {
            var Q0;
            Q0=makeQuery(id+"F16.imprint","IMPRINT",FACE,{"disambiguationData":[TD([[makeQuery(id+"F16.imprint","IMPRINT",EDGE,{"derivedFrom":sQuery(id+"F16.wireOp",EDGE,"E82")}),-1.0]])]});
            var Q1;
            {var subQ0=sQuery(id+"F16.wireOp",EDGE,"E89.MirrorCS");Q1=makeQuery(id+"F16.imprint","IMPRINT",FACE,{"disambiguationData":[TD([[makeQuery(id+"F16.imprint","IMPRINT",EDGE,{"derivedFrom":subQ0}),-1.0]])]});}
            var Q2;
            {var subQ1=sQuery(id+"F16.wireOp",EDGE,"E79.1");Q2=makeQuery(id+"F16.imprint","IMPRINT",FACE,{"disambiguationData":[TD([[makeQuery(id+"F16.imprint","IMPRINT",EDGE,{"derivedFrom":subQ1}),1.0]])]});}
            var Q3;
            Q3=makeQuery(id+"F2.opExtrude","CAP_FACE",FACE,{"disambiguationData":[OSD([sQuery(id+"F0.wireOp",EDGE,"E12"),sQuery(id+"F0.wireOp",EDGE,"E13"),sQuery(id+"F0.wireOp",EDGE,"E14"),sQuery(id+"F0.wireOp",EDGE,"E15"),sQuery(id+"F0.wireOp",EDGE,"E17.filletArc"),sQuery(id+"F0.wireOp",EDGE,"E18.filletArc"),sQuery(id+"F0.wireOp",EDGE,"E19.filletArc"),sQuery(id+"F0.wireOp",EDGE,"E20.filletArc"),sQuery(id+"F0.wireOp",EDGE,"E25.0"),sQuery(id+"F0.wireOp",EDGE,"E25.1"),sQuery(id+"F0.wireOp",EDGE,"E25.2"),sQuery(id+"F0.wireOp",EDGE,"E25.3"),sQuery(id+"F0.wireOp",EDGE,"E25.4"),sQuery(id+"F0.wireOp",EDGE,"E25.5"),sQuery(id+"F0.wireOp",EDGE,"E25.6"),sQuery(id+"F0.wireOp",EDGE,"E25.7")])],"isStart":false});
            extrude(context, id + "F17", {"entities" : qUnion([Q0, Q1, Q2]), "endBound" : BoundingType.UP_TO_SURFACE, "endBoundEntityFace" : qUnion([Q3]), "depth" : 25 * mm});
        }
    });
